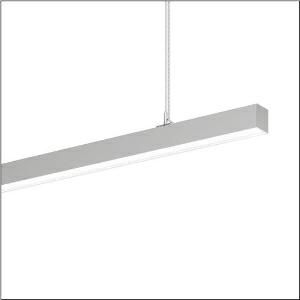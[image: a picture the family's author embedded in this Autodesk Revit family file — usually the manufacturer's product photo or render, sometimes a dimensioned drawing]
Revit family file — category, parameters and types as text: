
# Revit family: silica_r__21_51mx30db35sb_46d1
name_source: partatom
category: Lighting Fixtures
units: mm (PartAtom-declared; Revit-internal decimal feet)

## family parameters
Cut with Voids When Loaded = No
Host = Face
Light Source = No
Part Type = Normal
Room Calculation Point = No
Round Connector Dimension = Use Diameter
Shared = No

## types (1)
- --- (1 x LED, 5260 lm, 34.1 W, 3000K)
    Apparent Load = 34 VA
    CIE Flux Codes = 47 79 96 57 100
    Color Rendering = 80
    Color Temperature = 3000K
    Default Elevation = 1800 mm
    Description = Silica® 21, office luminaire, primary optical cover: cover, of PMMA, opal, light emission: direct/indirect distribution, primary light characteristic: symmetric, installation type: suspended mounting, LED, rated luminous flux: 5.260lm, luminous efficacy: 154lm/W, light colour: 830, colour temperature: 3000K, with terminal, 3+2-pole, max. 2.5mm², mains connection: 220..240V, AC, 50/60Hz, rated input power: 34.1W, luminaire housing, of aluminium, metallic grey (RAL 9006), length: 1.504mm, width: 53mm, height: 53mm, protection rating (complete): IP20, insulation class (complete): insulation class I (protective earthing), certification: CE, permissible operating ambient temperature: 0..+35°C, standard: EN 50419, packaging unit: 1 piece
    Height = 53 mm
    Lamp = 1 x LED
    Lamp Light Flux = 5260 lm
    Lamp Power = 34.1 W
    Lamp count = 1
    Length = 1504 mm
    Luminous efficacy = 154 lm/W
    Manufacturer = Siteco
    ModVariant = No
    Model = 51MX30DB35SB
    Mounting Place = Ceiling
    Mounting Type = Pendant
    Number of Poles = 1
    OnlyDefault = Yes
    Power Factor = 1
    Product Name = Silica® 21
    Product group = office luminaire | ceiling pendant
    ProductGroupID = 902
    Protection Class = Protection class I
    Protection Degree = IP 20
    RLX_Detail_Level = 1
    RLX_Emergency_Light_Flux = 0 lm
    RLX_Emergency_Type = 0
    RLX_Emergency_Type_DB = No
    RlxData = <blob elided: 23421 chars, md5=c36eaf14>
    Socket = socket
    Standby Power = 0 W
    System Light Flux = 5260 lm
    System Power = 34 W
    Type Comments = factory setting: luminous flux: 100 % | dim-lin: 254 | 233 mA
    Type Image = l_1313621.jpg
    URL = http://relux.com
    VarID = @adj_065091
    Voltage = 0 V
    Weight = 0.00 kg
    Width = 53 mm

## geometry (parser evidence)
native form markers: Blend x4, Sweep x12
no freeform markers — native parametric forms only
